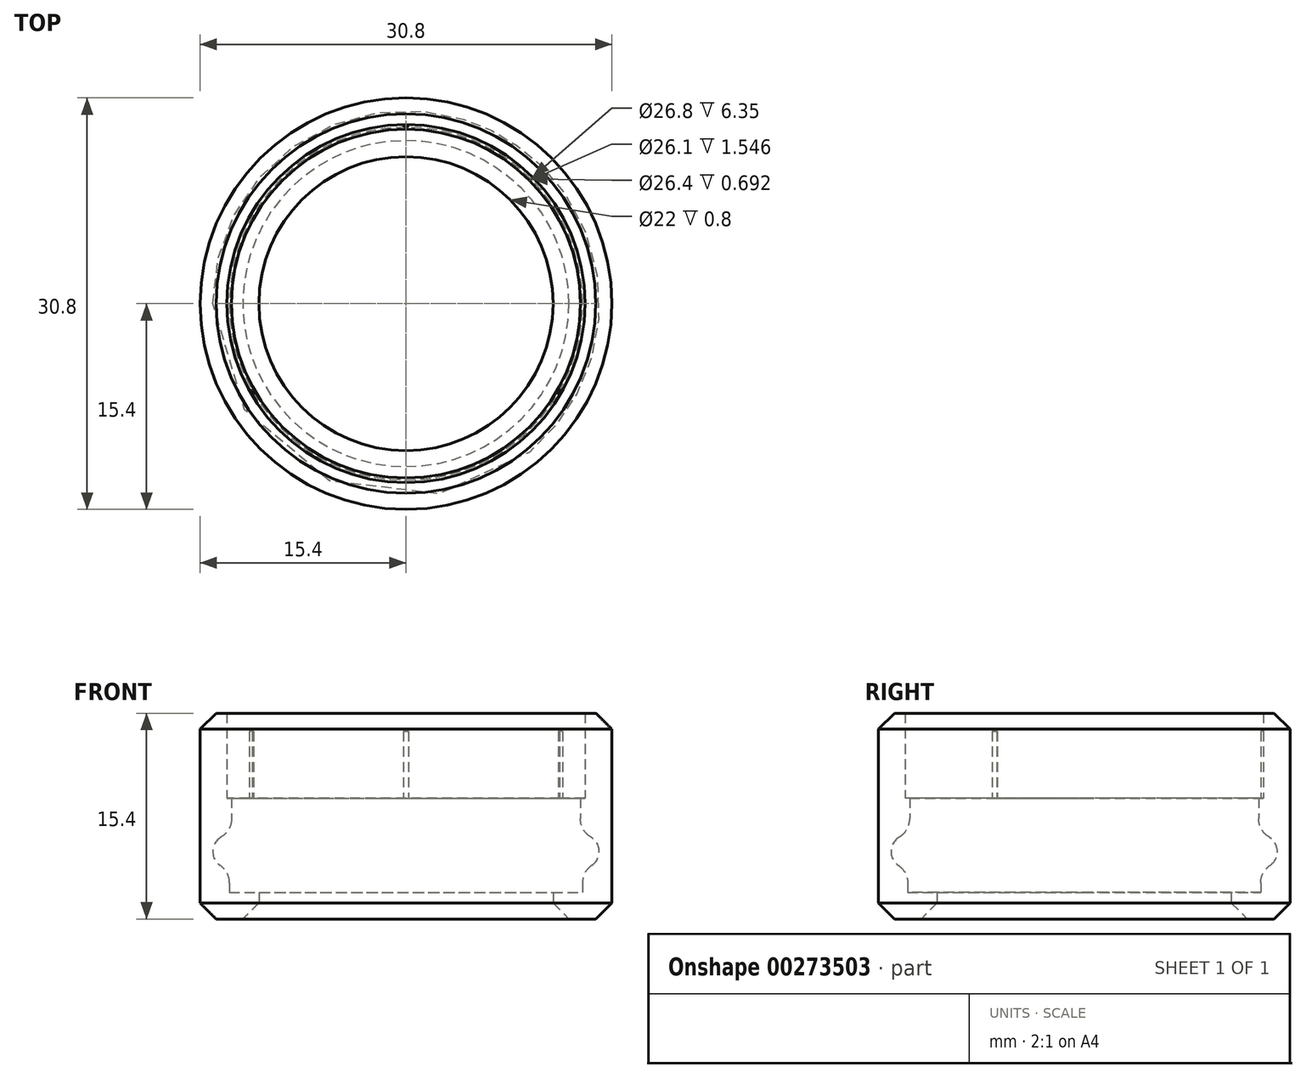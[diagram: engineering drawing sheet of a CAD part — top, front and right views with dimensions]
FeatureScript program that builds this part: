
annotation { "Feature Type Name" : "Feature", "Feature Type Description" : "" }
export const myFeature = defineFeature(function(context is Context, id is Id, definition is map)
    precondition{}
    {
        {
            var Q0;
            Q0=qCreatedBy(makeId("Front.planeOp"),FACE);
            var sketch = newSketch(context, id + "F0", { "sketchPlane" : qUnion([Q0])});
            skLineSegment(sketch, "E0", {"start": v(0, 0) * mm, "end": v(0, 18.8) * mm, "construction": true});
            skCircle(sketch, "E1", {"center": v(13.2, 5.05) * mm, "radius": 1.25 * mm});
            skLineSegment(sketch, "E2", {"start": v(13.05, 6.3) * mm, "end": v(13.05, 9.05) * mm});
            skLineSegment(sketch, "E3", {"start": v(13.4, 15.4) * mm, "end": v(13.4, 9.05) * mm});
            skLineSegment(sketch, "E4", {"start": v(13.4, 9.05) * mm, "end": v(13.05, 9.05) * mm});
            skLineSegment(sketch, "E5", {"start": v(11, 0) * mm, "end": v(11, 2) * mm});
            skLineSegment(sketch, "E6", {"start": v(11, 0) * mm, "end": v(15.4, 0) * mm});
            skLineSegment(sketch, "E7", {"start": v(15.4, 0) * mm, "end": v(15.4, 15.4) * mm});
            skLineSegment(sketch, "E8", {"start": v(15.4, 15.4) * mm, "end": v(13.4, 15.4) * mm});
            skLineSegment(sketch, "E9", {"start": v(11, 2) * mm, "end": v(13.2, 2) * mm});
            skLineSegment(sketch, "E10", {"start": v(13.2, 2) * mm, "end": v(13.2, 3.8) * mm});
            skSolve(sketch);
        }
        {
            var Q0;
            {var subQ0=sQuery(id+"F0.wireOp",EDGE,"5Dp9S94V-h94q-xsO0-CyC0-PU0V4zRin0x1");Q0=makeQuery(id+"F0.imprint","IMPRINT",FACE,{"disambiguationData":[TD([[makeQuery(id+"F0.imprint","IMPRINT",EDGE,{"derivedFrom":subQ0}),1.0]])]});}
            var Q1;
            {var subQ0=sQuery(id+"F0.wireOp",EDGE,"E2");Q1=makeQuery(id+"F0.imprint","IMPRINT",FACE,{"disambiguationData":[TD([[makeQuery(id+"F0.imprint","IMPRINT",EDGE,{"derivedFrom":subQ0}),-1.0]])]});}
            var Q2;
            Q2=sQuery(id+"F0.wireOp",EDGE,"E0");
            revolve(context, id + "F1", {"surfaceOperationType" : NewSurfaceOperationType.NEW, "entities" : qUnion([Q0, Q1]), "axis" : qUnion([Q2]), "revolveType" : RevolveType.FULL});
        }
        {
            var Q0;
            Q0=makeQuery(id+"F1.opRevolve","SWEPT_EDGE",EDGE,{"disambiguationData":[OSD([sQuery(id+"F0.wireOp",EDGE,"E5"),sQuery(id+"F0.wireOp",EDGE,"E6")])]});
            var Q1;
            Q1=makeQuery(id+"F1.opRevolve","SWEPT_EDGE",EDGE,{"disambiguationData":[OSD([sQuery(id+"F0.wireOp",EDGE,"E6"),sQuery(id+"F0.wireOp",EDGE,"E7")])]});
            var Q2;
            Q2=makeQuery(id+"F1.opRevolve","SWEPT_EDGE",EDGE,{"disambiguationData":[OSD([sQuery(id+"F0.wireOp",EDGE,"E7"),sQuery(id+"F0.wireOp",EDGE,"E8")])]});
            chamfer(context, id + "F2", {"entities" : qUnion([Q0, Q1, Q2]), "width" : 1.2 * mm, "tangentPropagation" : true});
        }
        {
            var Q0;
            Q0=makeQuery(id+"F1.opRevolve","SWEPT_EDGE",EDGE,{"disambiguationData":[OSD([sQuery(id+"F0.wireOp",EDGE,"E1"),sQuery(id+"F0.wireOp",EDGE,"E2")])]});
            var Q1;
            Q1=makeQuery(id+"F1.opRevolve","SWEPT_EDGE",EDGE,{"disambiguationData":[OSD([sQuery(id+"F0.wireOp",EDGE,"E1"),sQuery(id+"F0.wireOp",EDGE,"E10")])]});
            fillet(context, id + "F3", {"entities" : qUnion([Q0, Q1]), "radius" : 1.6 * mm, "tangentPropagation" : true, "allowEdgeOverflow" : false});
        }
        {
            var Q0;
            Q0=makeQuery(id+"F1.opRevolve","SWEPT_FACE",FACE,{"disambiguationData":[OSD([sQuery(id+"F0.wireOp",EDGE,"E4")])]});
            var sketch = newSketch(context, id + "F4", { "sketchPlane" : qUnion([Q0])});
            skCircle(sketch, "E11", {"center": v(0, 13.4) * mm, "radius": 0.2 * mm});
            skCircle(sketch, "E12.1.0", {"center": v(-11.6, -6.7) * mm, "radius": 0.2 * mm});
            skCircle(sketch, "E12.2.0", {"center": v(11.6, -6.7) * mm, "radius": 0.2 * mm});
            skPoint(sketch, "E12.center", {"position": v(0, 0) * mm});
            skSolve(sketch);
        }
        {
            var Q0;
            {var subQ0=sQuery(id+"F4.wireOp",EDGE,"E12.1.0");var subQ1=makeQuery(id+"F1.opRevolve","SWEPT_EDGE",EDGE,{"disambiguationData":[OSD([sQuery(id+"F0.wireOp",EDGE,"E3"),sQuery(id+"F0.wireOp",EDGE,"E4")])]});var subQ2=makeQuery(id+"F4.imprint","INTERSECT",VERTEX,{"disambiguationData":[OD(0.0)],"derivedFrom":[subQ1,subQ0]});Q0=makeQuery(id+"F4.imprint","IMPRINT",FACE,{"disambiguationData":[TD([[makeQuery(id+"F4.imprint","IMPRINT",EDGE,{"disambiguationData":[TD([[subQ2,1.0]])],"derivedFrom":subQ0}),1.0]])]});}
            var Q1;
            {var subQ0=sQuery(id+"F4.wireOp",EDGE,"E11");var subQ1=makeQuery(id+"F1.opRevolve","SWEPT_EDGE",EDGE,{"disambiguationData":[OSD([sQuery(id+"F0.wireOp",EDGE,"E3"),sQuery(id+"F0.wireOp",EDGE,"E4")])]});var subQ2=makeQuery(id+"F4.imprint","INTERSECT",VERTEX,{"disambiguationData":[OD(0.0)],"derivedFrom":[subQ1,subQ0]});Q1=makeQuery(id+"F4.imprint","IMPRINT",FACE,{"disambiguationData":[TD([[makeQuery(id+"F4.imprint","IMPRINT",EDGE,{"disambiguationData":[TD([[subQ2,-1.0]])],"derivedFrom":subQ0}),1.0]])]});}
            var Q2;
            {var subQ0=sQuery(id+"F4.wireOp",EDGE,"E12.2.0");var subQ1=makeQuery(id+"F1.opRevolve","SWEPT_EDGE",EDGE,{"disambiguationData":[OSD([sQuery(id+"F0.wireOp",EDGE,"E3"),sQuery(id+"F0.wireOp",EDGE,"E4")])]});var subQ2=makeQuery(id+"F4.imprint","INTERSECT",VERTEX,{"disambiguationData":[OD(0.0)],"derivedFrom":[subQ1,subQ0]});Q2=makeQuery(id+"F4.imprint","IMPRINT",FACE,{"disambiguationData":[TD([[makeQuery(id+"F4.imprint","IMPRINT",EDGE,{"disambiguationData":[TD([[subQ2,1.0]])],"derivedFrom":subQ0}),1.0]])]});}
            extrude(context, id + "F5", {"entities" : qUnion([Q0, Q1, Q2]), "operationType" : NewBodyOperationType.ADD, "depth" : 5 * mm, "offsetDistance" : 25 * mm});
        }
    });
